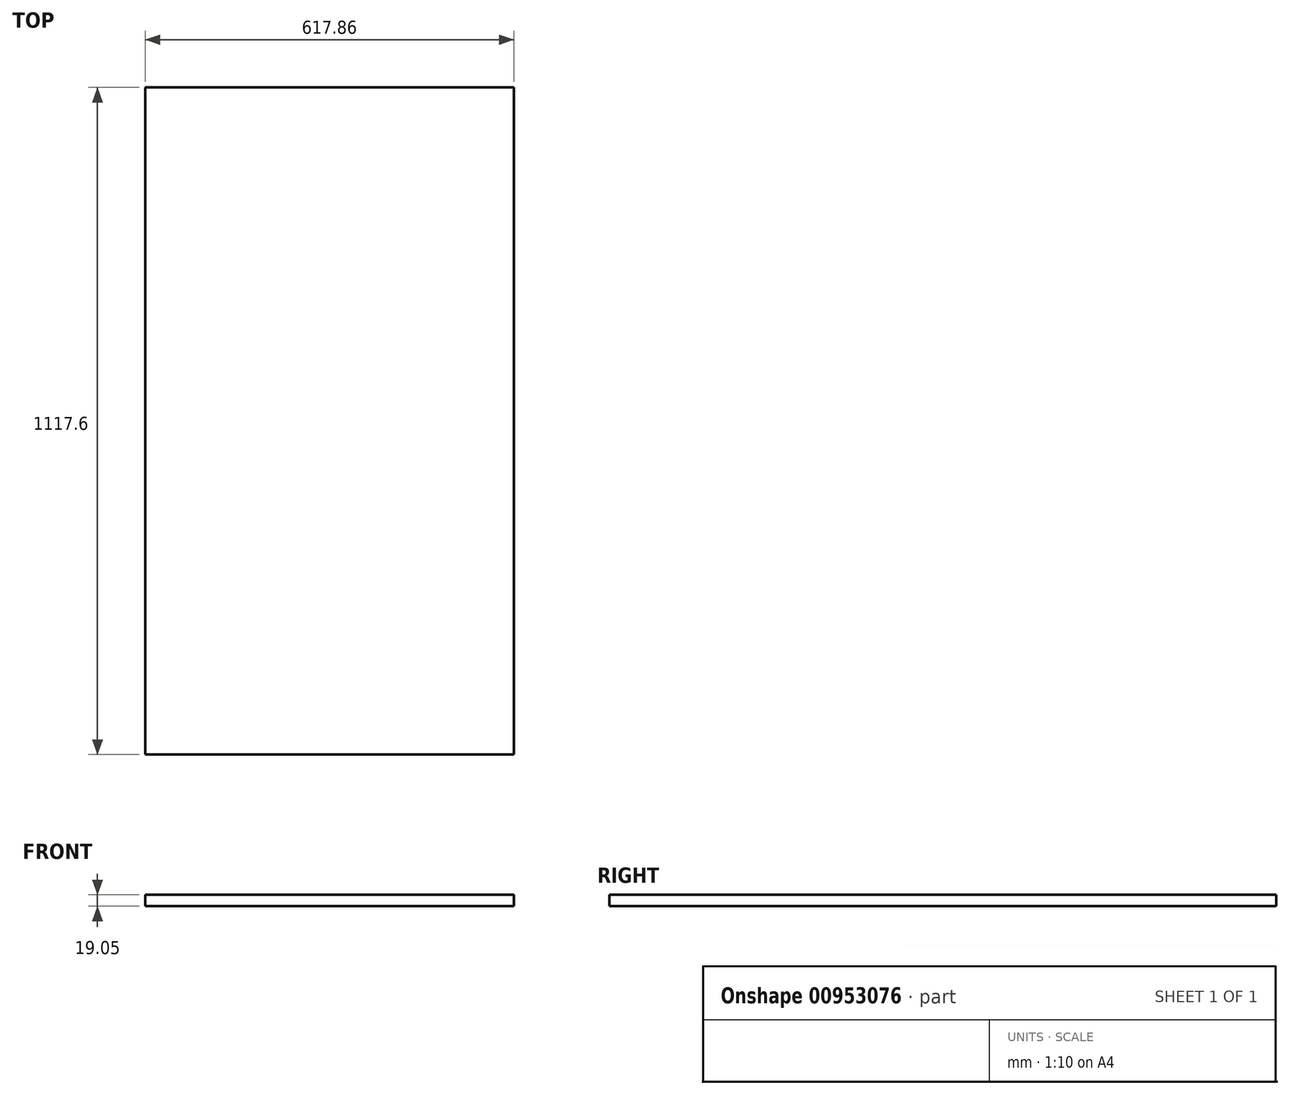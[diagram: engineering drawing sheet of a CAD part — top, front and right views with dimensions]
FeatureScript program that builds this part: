
annotation { "Feature Type Name" : "Feature", "Feature Type Description" : "" }
export const myFeature = defineFeature(function(context is Context, id is Id, definition is map)
    precondition{}
    {
        {
            var Q0;
            Q0=qCreatedBy(makeId("Top.planeOp"),FACE);
            var sketch = newSketch(context, id + "F0", { "sketchPlane" : qUnion([Q0])});
            skLineSegment(sketch, "E0", {"start": v(0, 0) * mm, "end": v(-617.86, 0) * mm});
            skLineSegment(sketch, "E1", {"start": v(-617.86, 0) * mm, "end": v(-617.86, 1117.6) * mm});
            skLineSegment(sketch, "E2", {"start": v(-617.86, 1117.6) * mm, "end": v(0, 1117.6) * mm});
            skLineSegment(sketch, "E3", {"start": v(0, 1117.6) * mm, "end": v(0, 0) * mm});
            skSolve(sketch);
        }
        {
            var Q0;
            Q0 = qSketchRegion(id + "F0", true);
            extrude(context, id + "F1", {"entities" : qUnion([Q0]), "depth" : 19.05 * mm, "offsetDistance" : 25.4 * mm});
        }
    });
